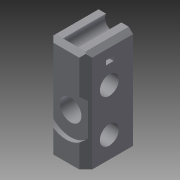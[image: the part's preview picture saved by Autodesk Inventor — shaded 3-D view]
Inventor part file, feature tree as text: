
AUTODESK INVENTOR PART (.ipt)
format: ipt  version: 2015 (Build 190159000, 159)  size: 159,744 bytes
history: native  units: mm
features: sketch x6, chamfer x5, extrude x3, hole x3
ambient origin geometry x8: Origin, YZ Plane, XZ Plane, XY Plane, X Axis, Y Axis, Z Axis, Center Point
bodies: Solid1 (feature_tree)
feature tree (17):
  extrude  "Extrusion1"  Depth=22.0mm
  hole  "Hole3"  [1 undecoded]
  hole  "Hole4"  [1 undecoded]
  chamfer  "Chamfer1"  Distance=2.0mm Angle=45.0deg
  chamfer  "Chamfer2"  Distance=2.0mm Angle=45.0deg
  chamfer  "Chamfer3"  Distance=2.0mm Angle=45.0deg
  chamfer  "Chamfer4"  Distance=2.0mm Angle=45.0deg
  chamfer  "Chamfer5"  Distance=2.0mm Angle=45.0deg
  hole  "Hole5"  [1 undecoded]
  extrude  "Extrusion4"  Depth=3.5mm
  extrude  "Extrusion5"  Depth=6.325mm
  sketch  "Sketch1"  dims[d0=18.0mm d1=22.0mm]
  sketch  "Sketch3"  dims[d2=47.0mm d3=0.0mm]
  sketch  "Sketch4"  dims[d22=8.0mm d23=6.0mm d24=4.0mm d25=2.0mm d26=90.0deg d27=20.0mm d28=0.0mm d31=1.8mm]
  sketch  "Sketch6"  dims[d33=17.0mm]
  sketch  "Sketch7"  dims[d34=8.8mm d35=6.0mm d36=4.0mm d37=2.0mm d38=90.0deg d39=8.0mm d40=20.594885mm d42=20.0mm d43=3.0mm d44=2.0mm d45=45.0deg d46=3.0mm d47=2.0mm d48=45.0deg d49=2.0mm d50=2.0mm d51=45.0deg d52=2.0mm d53=2.0mm d54=45.0deg d55=2.0mm d56=2.0mm d57=45.0deg]
  sketch  "Sketch8"  dims[d67=20.0mm d68=10.0mm d69=6.0mm d70=22.0mm d71=2.0mm d72=90.0deg d73=8.0mm d74=20.594885mm d75=2.0mm d76=3.5mm d77=6.325mm d78=9.487mm d79=10.0mm d80=0.0mm d81=2.0mm d82=3.5mm d83=9.0mm d85=8.0mm d86=8.0mm d87=0.0mm]
note: 3 required parameter values undecoded (feature->parameter linkage not recoverable at this tier; creation-order binding heuristic only, values carry confidence <= 0.55)
